# Revit family: NLRS_33_GM_FB_TC_STORAX_vloerluik_DeMaxx_BCB
name_source: partatom
category: Generic Models
revit_build: Autodesk Revit 2015 (Build: 20140223_1515(x64)
units: mm (PartAtom-declared; Revit-internal decimal feet)

## types (3) — shared parameters
Manufacturer = Storax
Model = De-Maxx
URL = http://www.storax.nl
bediening = handmatig
belasting kg/m2 = 200
brandwerend 120 min = No
brandwerend 30 min = No
brandwerend 60 min = No
cilinderslot = Yes
code productgroep = LUI
conservering = RAL 7047
deurblad = vlak
garantietermijn in jaren = 10
gewicht = 92.00 kg
hoogte = 310 mm  [stored 1.01706 ft]
isolatie = Yes
isolatiedikte = 140 mm
isolatiewaarde = 6.3500 (m²·K)/W
loopslot = No
luchtdoorlatendheid 600 Pa = EN1026-klasse 4 , EN12207
materiaal = bcb_aluminium
modeler = Bouwconnect
normering = EN-14351-1
omranding waterafvoerend = No
omschrijving = standaard aluminium dakluik
openingshoek = 90.00°
openstand vergrendeling = Yes
plaatdikte = 2 mm  [stored 0.00656168 ft]
productgroep = Dakluiken
scharnierend = Yes
thermische onderbreking = Yes
veersysteem = Yes
vuilafdichting = No
waterdicht = Yes
waterdichtheid 600 Pa = EN1027-klasse9A EN12208
windweerstand = EN12211-klasse C5, EN 12210
zero-valued in all types: Default Elevation

## per-type parameters (varying)
| type | binnenmaat_breedte | binnenmaat_lengte | uitwendige_breedte | uitwendige_lengte |
| De-Maxx 70/90 | 700 mm | 900 mm  [stored 2.95276 ft] | 1080 mm  [stored 3.54331 ft] | 1280 mm |
| De-Maxx 90/90 | 900 mm  [stored 2.95276 ft] | 900 mm  [stored 2.95276 ft] | 1280 mm | 1280 mm |
| De-Maxx 70/140 | 700 mm | 1400 mm  [stored 4.59318 ft] | 1080 mm  [stored 3.54331 ft] | 1780 mm  [stored 5.8399 ft] |

note: [stored X ft] marks values corroborated as IEEE doubles in the binary element streams (Revit-internal decimal feet)

## geometry (parser evidence)
native form markers: Blend x765, Sweep x15
no freeform markers — native parametric forms only
